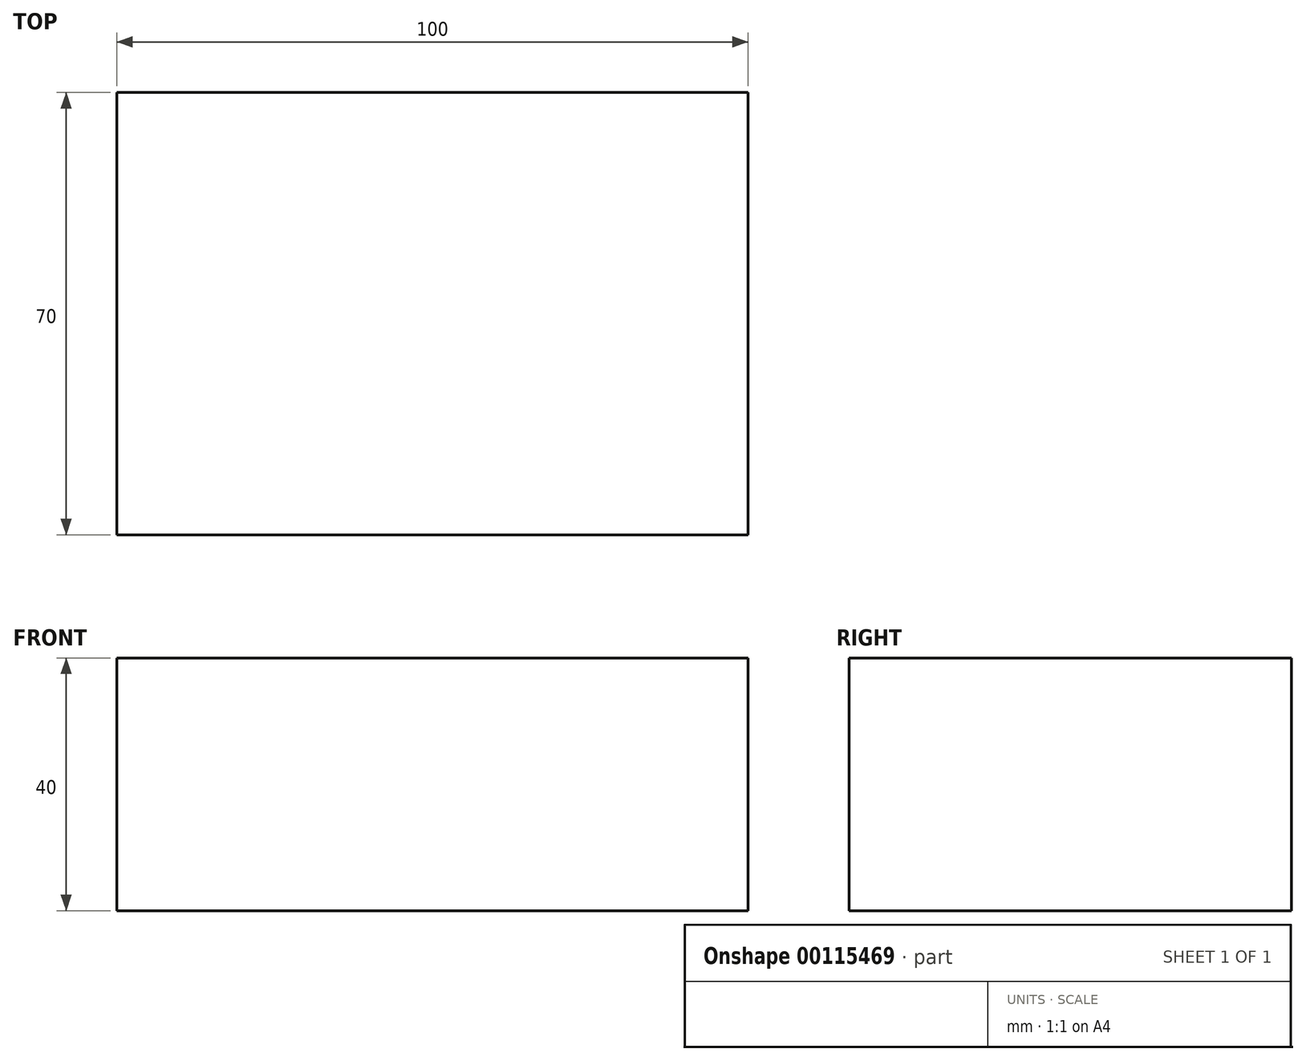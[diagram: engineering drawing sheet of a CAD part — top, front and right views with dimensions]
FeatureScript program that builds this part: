
annotation { "Feature Type Name" : "Feature", "Feature Type Description" : "" }
export const myFeature = defineFeature(function(context is Context, id is Id, definition is map)
    precondition{}
    {
        {
            var Q0;
            Q0=qCreatedBy(makeId("Top.planeOp"),FACE);
            var sketch = newSketch(context, id + "F0", { "sketchPlane" : qUnion([Q0])});
            skLineSegment(sketch, "E0.bottom", {"start": v(-74, 38.29) * mm, "end": v(26, 38.29) * mm});
            skLineSegment(sketch, "E0.top", {"start": v(-74, -31.71) * mm, "end": v(26, -31.71) * mm});
            skLineSegment(sketch, "E0.left", {"start": v(-74, 38.29) * mm, "end": v(-74, -31.71) * mm});
            skLineSegment(sketch, "E0.right", {"start": v(26, 38.29) * mm, "end": v(26, -31.71) * mm});
            skSolve(sketch);
        }
        {
            var Q0;
            Q0=makeQuery(id+"F0.imprint","IMPRINT",FACE,{"disambiguationData":[TD([[makeQuery(id+"F0.imprint","IMPRINT",EDGE,{"derivedFrom":sQuery(id+"F0.wireOp",EDGE,"E0.bottom")}),-1.0]])]});
            extrude(context, id + "F1", {"entities" : qUnion([Q0]), "depth" : 40 * mm});
        }
    });
